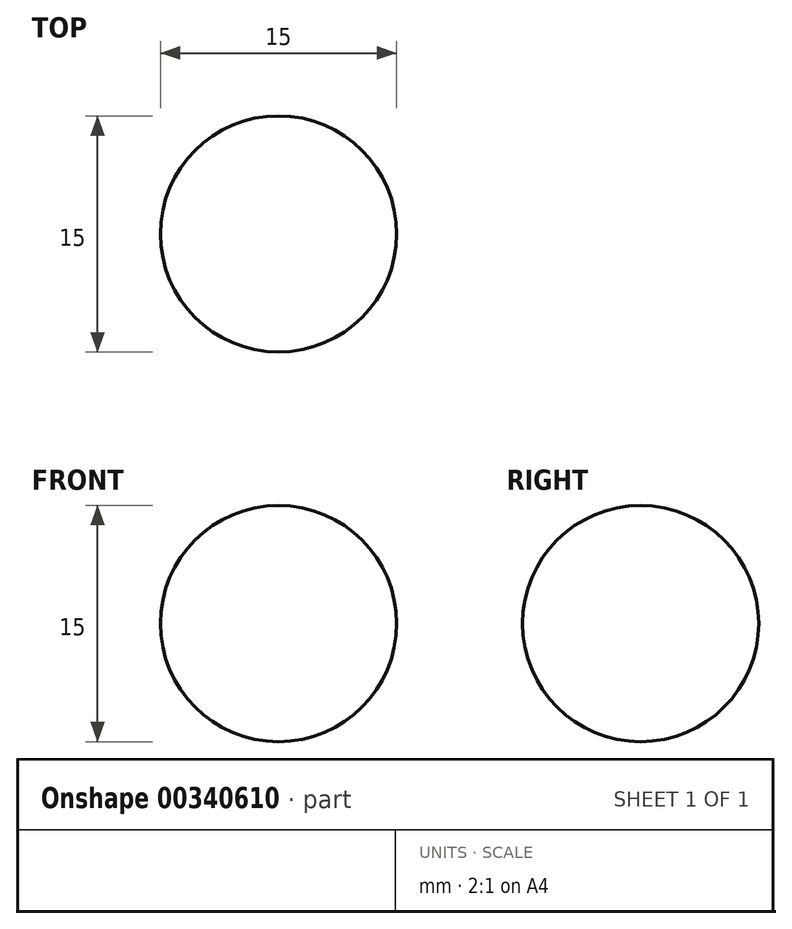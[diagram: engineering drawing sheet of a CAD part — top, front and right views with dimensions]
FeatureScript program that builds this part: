
annotation { "Feature Type Name" : "Feature", "Feature Type Description" : "" }
export const myFeature = defineFeature(function(context is Context, id is Id, definition is map)
    precondition{}
    {
        {
            var Q0;
            Q0=qCreatedBy(makeId("Front.planeOp"),FACE);
            var sketch = newSketch(context, id + "F0", { "sketchPlane" : qUnion([Q0])});
            skArc(sketch, "E0", {"start": v(0, -7.5) * mm, "mid": v(7.5, 0) * mm, "end": v(0, 7.5) * mm});
            skLineSegment(sketch, "E1", {"start": v(0, 7.5) * mm, "end": v(0, -7.5) * mm});
            skSolve(sketch);
        }
        {
            var Q0;
            Q0=makeQuery(id+"F0.imprint","IMPRINT",FACE,{"disambiguationData":[TD([[makeQuery(id+"F0.imprint","IMPRINT",EDGE,{"derivedFrom":sQuery(id+"F0.wireOp",EDGE,"E0")}),1.0]])]});
            var Q1;
            Q1=sQuery(id+"F0.wireOp",EDGE,"E1");
            revolve(context, id + "F1", {"entities" : qUnion([Q0]), "axis" : qUnion([Q1]), "revolveType" : RevolveType.FULL});
        }
    });
